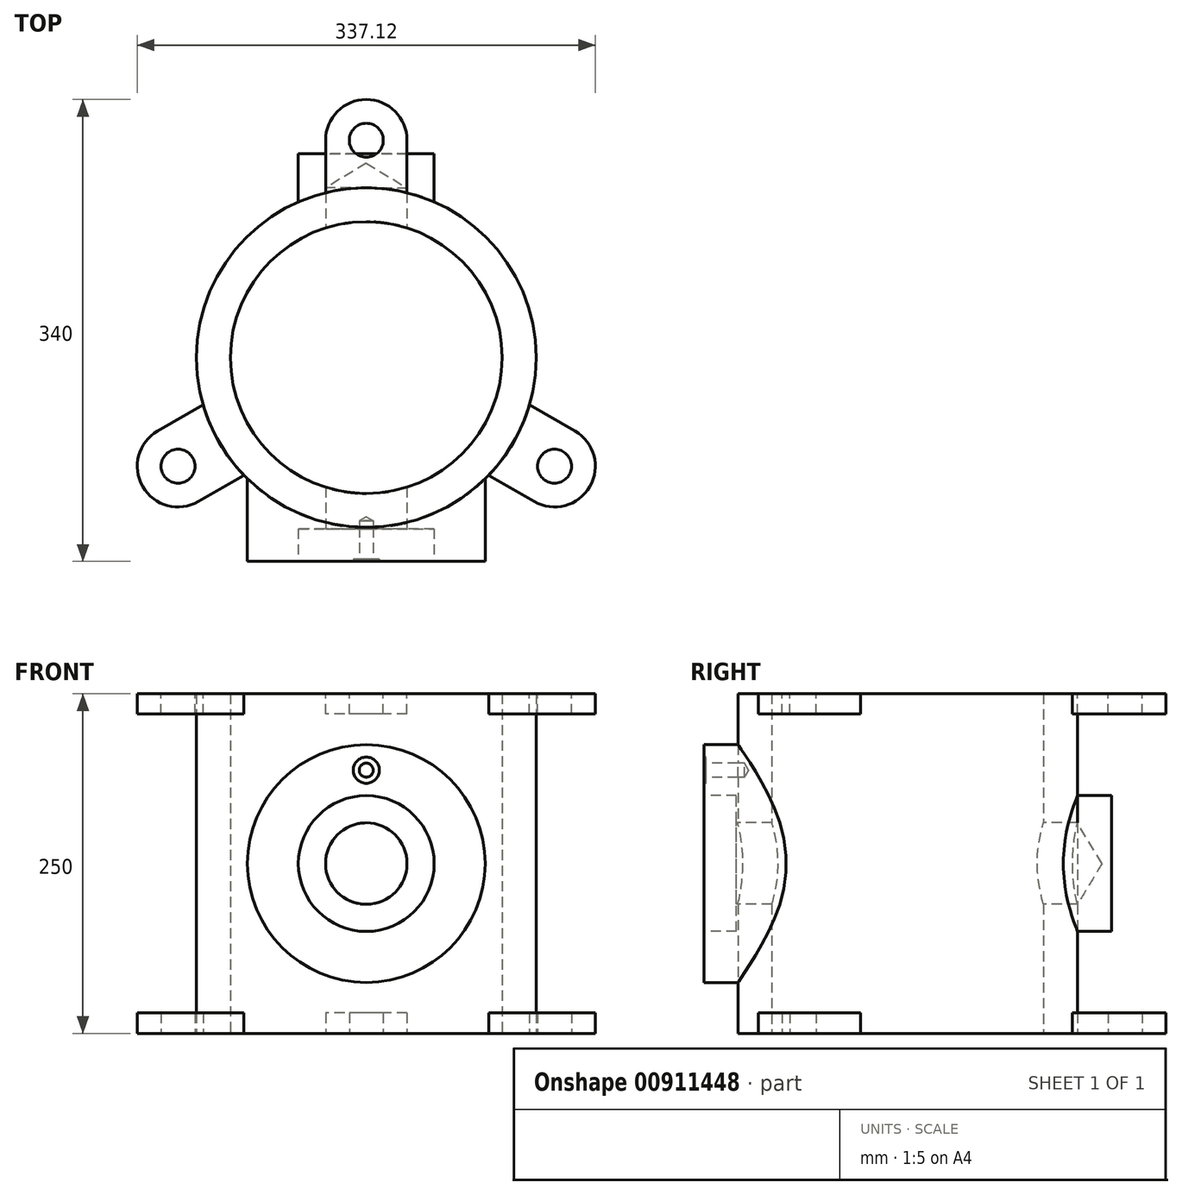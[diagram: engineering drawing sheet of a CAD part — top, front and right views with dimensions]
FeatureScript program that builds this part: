
annotation { "Feature Type Name" : "Feature", "Feature Type Description" : "" }
export const myFeature = defineFeature(function(context is Context, id is Id, definition is map)
    precondition{}
    {
        {
            var Q0;
            Q0=qCreatedBy(makeId("Top.planeOp"),FACE);
            var sketch = newSketch(context, id + "F0", { "sketchPlane" : qUnion([Q0])});
            skCircle(sketch, "E0", {"center": v(0, 0) * mm, "radius": 100 * mm});
            skCircle(sketch, "E1", {"center": v(0, 0) * mm, "radius": 125 * mm});
            skSolve(sketch);
        }
        {
            var Q0;
            Q0=makeQuery(id+"F0.imprint","IMPRINT",FACE,{"disambiguationData":[TD([[makeQuery(id+"F0.imprint","IMPRINT",EDGE,{"derivedFrom":sQuery(id+"F0.wireOp",EDGE,"E0")}),-1.0]])]});
            extrude(context, id + "F1", {"entities" : qUnion([Q0]), "depth" : 250 * mm, "offsetDistance" : 25 * mm, "symmetric" : true});
        }
        {
            var Q0;
            Q0=makeQuery(id+"F1.opExtrude","CAP_FACE",FACE,{"disambiguationData":[OSD([sQuery(id+"F0.wireOp",EDGE,"E0"),sQuery(id+"F0.wireOp",EDGE,"E1")])],"isStart":false});
            var sketch = newSketch(context, id + "F2", { "sketchPlane" : qUnion([Q0])});
            skLineSegment(sketch, "E2", {"start": v(0, 0) * mm, "end": v(0, 160) * mm, "construction": true});
            skCircle(sketch, "E3", {"center": v(0, 160) * mm, "radius": 12.5 * mm});
            skArc(sketch, "E4", {"start": v(-30, 160) * mm, "mid": v(0, 190) * mm, "end": v(30, 160) * mm});
            skLineSegment(sketch, "E5", {"start": v(30, 160) * mm, "end": v(30, 121.35) * mm});
            skLineSegment(sketch, "E6", {"start": v(-30, 160) * mm, "end": v(-30, 121.35) * mm});
            skLineSegment(sketch, "E7.1.0", {"start": v(-123.56, -105.98) * mm, "end": v(-90.09, -86.65) * mm});
            skCircle(sketch, "E7.1.1", {"center": v(-138.56, -80) * mm, "radius": 12.5 * mm});
            skLineSegment(sketch, "E7.1.2", {"start": v(-153.56, -54.02) * mm, "end": v(-120.09, -34.7) * mm});
            skArc(sketch, "E7.1.3", {"start": v(-123.56, -105.98) * mm, "mid": v(-164.54, -95) * mm, "end": v(-153.56, -54.02) * mm});
            skLineSegment(sketch, "E7.2.0", {"start": v(153.56, -54.02) * mm, "end": v(120.09, -34.7) * mm});
            skCircle(sketch, "E7.2.1", {"center": v(138.56, -80) * mm, "radius": 12.5 * mm});
            skLineSegment(sketch, "E7.2.2", {"start": v(123.56, -105.98) * mm, "end": v(90.09, -86.65) * mm});
            skArc(sketch, "E7.2.3", {"start": v(153.56, -54.02) * mm, "mid": v(164.54, -95) * mm, "end": v(123.56, -105.98) * mm});
            skPoint(sketch, "E7.center", {"position": v(0, 0) * mm});
            skSolve(sketch);
        }
        {
            var Q0;
            Q0=makeQuery(id+"F2.imprint","IMPRINT",FACE,{"disambiguationData":[TD([[makeQuery(id+"F2.imprint","IMPRINT",EDGE,{"derivedFrom":sQuery(id+"F2.wireOp",EDGE,"E3")}),-1.0]])]});
            var Q1;
            {var subQ1=sQuery(id+"F2.wireOp",EDGE,"E7.1.0");Q1=makeQuery(id+"F2.imprint","IMPRINT",FACE,{"disambiguationData":[TD([[makeQuery(id+"F2.imprint","IMPRINT",EDGE,{"derivedFrom":subQ1}),1.0]])]});}
            var Q2;
            {var subQ1=sQuery(id+"F2.wireOp",EDGE,"E7.2.0");Q2=makeQuery(id+"F2.imprint","IMPRINT",FACE,{"disambiguationData":[TD([[makeQuery(id+"F2.imprint","IMPRINT",EDGE,{"derivedFrom":subQ1}),1.0]])]});}
            extrude(context, id + "F3", {"entities" : qUnion([Q0, Q1, Q2]), "oppositeDirection" : true, "depth" : 15 * mm, "offsetDistance" : 25 * mm});
        }
        {
            var Q0;
            Q0=makeQuery(id+"F3.opExtrude","SWEPT_BODY",BODY,{"disambiguationData":[OSD([sQuery(id+"F0.wireOp",EDGE,"E1"),sQuery(id+"F2.wireOp",EDGE,"E3"),sQuery(id+"F2.wireOp",EDGE,"E4"),sQuery(id+"F2.wireOp",EDGE,"E5"),sQuery(id+"F2.wireOp",EDGE,"E6")])]});
            var Q1;
            Q1=makeQuery(id+"F3.opExtrude","SWEPT_BODY",BODY,{"disambiguationData":[OSD([sQuery(id+"F0.wireOp",EDGE,"E1"),sQuery(id+"F2.wireOp",EDGE,"E7.1.0"),sQuery(id+"F2.wireOp",EDGE,"E7.1.1"),sQuery(id+"F2.wireOp",EDGE,"E7.1.2"),sQuery(id+"F2.wireOp",EDGE,"E7.1.3")])]});
            var Q2;
            Q2=makeQuery(id+"F3.opExtrude","SWEPT_BODY",BODY,{"disambiguationData":[OSD([sQuery(id+"F0.wireOp",EDGE,"E1"),sQuery(id+"F2.wireOp",EDGE,"E7.2.0"),sQuery(id+"F2.wireOp",EDGE,"E7.2.1"),sQuery(id+"F2.wireOp",EDGE,"E7.2.2"),sQuery(id+"F2.wireOp",EDGE,"E7.2.3")])]});
            var Q3;
            Q3=qCreatedBy(makeId("Top.planeOp"),FACE);
            mirror(context, id + "F4", {"entities" : qUnion([Q0, Q1, Q2]), "mirrorPlane" : qUnion([Q3])});
        }
        {
            var Q0;
            Q0=qCreatedBy(makeId("Front.planeOp"),FACE);
            cPlane(context, id + "F5", {"entities" : qUnion([Q0]), "cplaneType" : CPlaneType.OFFSET, "offset" : 150 * mm, "width" : 150 * mm, "height" : 150 * mm});
        }
        {
            var Q0;
            Q0=qCreatedBy(id+"F5.planeOp",FACE);
            var sketch = newSketch(context, id + "F6", { "sketchPlane" : qUnion([Q0])});
            skCircle(sketch, "E8", {"center": v(0, 0) * mm, "radius": 87.5 * mm});
            skSolve(sketch);
        }
        {
            var Q0;
            Q0=makeQuery(id+"F6.imprint","IMPRINT",FACE,{"disambiguationData":[TD([[makeQuery(id+"F6.imprint","IMPRINT",EDGE,{"derivedFrom":sQuery(id+"F6.wireOp",EDGE,"E8")}),1.0]])]});
            extrude(context, id + "F7", {"entities" : qUnion([Q0]), "endBound" : BoundingType.UP_TO_NEXT, "oppositeDirection" : true, "depth" : 25 * mm, "offsetDistance" : 25 * mm});
        }
        {
            var Q0;
            Q0=qCreatedBy(makeId("Front.planeOp"),FACE);
            cPlane(context, id + "F8", {"entities" : qUnion([Q0]), "cplaneType" : CPlaneType.OFFSET, "offset" : 150 * mm, "oppositeDirection" : true, "width" : 150 * mm, "height" : 150 * mm});
        }
        {
            var Q0;
            Q0=qCreatedBy(id+"F8.planeOp",FACE);
            var sketch = newSketch(context, id + "F9", { "sketchPlane" : qUnion([Q0])});
            skCircle(sketch, "E9", {"center": v(0, 0) * mm, "radius": 50 * mm});
            skSolve(sketch);
        }
        {
            var Q0;
            Q0=makeQuery(id+"F9.imprint","IMPRINT",FACE,{"disambiguationData":[TD([[makeQuery(id+"F9.imprint","IMPRINT",EDGE,{"derivedFrom":sQuery(id+"F9.wireOp",EDGE,"E9")}),1.0]])]});
            extrude(context, id + "F10", {"entities" : qUnion([Q0]), "endBound" : BoundingType.UP_TO_NEXT, "depth" : 25 * mm, "offsetDistance" : 25 * mm});
        }
        {
            var Q0;
            Q0=qCreatedBy(id+"F5.planeOp",FACE);
            var sketch = newSketch(context, id + "F11", { "sketchPlane" : qUnion([Q0])});
            skPoint(sketch, "E10", {"position": v(0, 0) * mm});
            skPoint(sketch, "E11", {"position": v(0, 68.75) * mm});
            skSolve(sketch);
        }
        {
            var Q0;
            Q0=sQuery(id+"F11.wireOp",VERTEX,"E10");
            var Q1;
            Q1=makeQuery(id+"F1.opExtrude","SWEPT_BODY",BODY,{"disambiguationData":[OSD([sQuery(id+"F0.wireOp",EDGE,"E0"),sQuery(id+"F0.wireOp",EDGE,"E1")])]});
            var Q2;
            Q2=makeQuery(id+"FjgMNlp9pOEb26B_1.1.F1.opExtrude","SWEPT_BODY",BODY,{"disambiguationData":[OSD([sQuery(id+"F0.wireOp",EDGE,"E0"),sQuery(id+"F0.wireOp",EDGE,"E1")])]});
            var Q3;
            Q3=makeQuery(id+"FjgMNlp9pOEb26B_1.2.F1.opExtrude","SWEPT_BODY",BODY,{"disambiguationData":[OSD([sQuery(id+"F0.wireOp",EDGE,"E0"),sQuery(id+"F0.wireOp",EDGE,"E1")])]});
            var Q4;
            Q4=makeQuery(id+"F7.opExtrude","SWEPT_BODY",BODY,{"disambiguationData":[OSD([sQuery(id+"F6.wireOp",EDGE,"E8")])]});
            var Q5;
            Q5=makeQuery(id+"F10.opExtrude","SWEPT_BODY",BODY,{"disambiguationData":[OSD([sQuery(id+"F9.wireOp",EDGE,"E9")])]});
            hole(context, id + "F12", {"style" : HoleStyle.C_BORE, "endStyle" : HoleEndStyle.BLIND, "holeDiameter" : 60 * mm, "cBoreDiameter" : 100 * mm, "cBoreDepth" : 24 * mm, "majorDiameter" : 5 * mm, "holeDepth" : 275 * mm, "isTappedThrough" : true, "tappedDepth" : 12 * mm, "tapClearance" : 3, "locations" : qUnion([Q0]), "scope" : qUnion([Q1, Q2, Q3, Q4, Q5])});
        }
        {
            var Q0;
            Q0=qCreatedBy(id+"F5.planeOp",FACE);
            var sketch = newSketch(context, id + "F13", { "sketchPlane" : qUnion([Q0])});
            skPoint(sketch, "E12", {"position": v(0, 0) * mm});
            skPoint(sketch, "E13", {"position": v(0, 68.75) * mm});
            skSolve(sketch);
        }
        {
            var Q0;
            Q0=sQuery(id+"F13.wireOp",VERTEX,"E13");
            var Q1;
            Q1=makeQuery(id+"F1.opExtrude","SWEPT_BODY",BODY,{"disambiguationData":[OSD([sQuery(id+"F0.wireOp",EDGE,"E0"),sQuery(id+"F0.wireOp",EDGE,"E1")])]});
            var Q2;
            Q2=makeQuery(id+"FjgMNlp9pOEb26B_1.1.F1.opExtrude","SWEPT_BODY",BODY,{"disambiguationData":[OSD([sQuery(id+"F0.wireOp",EDGE,"E0"),sQuery(id+"F0.wireOp",EDGE,"E1")])]});
            var Q3;
            Q3=makeQuery(id+"FjgMNlp9pOEb26B_1.2.F1.opExtrude","SWEPT_BODY",BODY,{"disambiguationData":[OSD([sQuery(id+"F0.wireOp",EDGE,"E0"),sQuery(id+"F0.wireOp",EDGE,"E1")])]});
            var Q4;
            Q4=makeQuery(id+"F7.opExtrude","SWEPT_BODY",BODY,{"disambiguationData":[OSD([sQuery(id+"F6.wireOp",EDGE,"E8")])]});
            hole(context, id + "F14", {"style" : HoleStyle.C_BORE, "endStyle" : HoleEndStyle.BLIND, "holeDiameter" : 10.3 * mm, "cBoreDiameter" : 19.25 * mm, "cBoreDepth" : 1.75 * mm, "majorDiameter" : 5 * mm, "holeDepth" : 29.75 * mm, "isTappedThrough" : true, "tappedDepth" : 12 * mm, "tapClearance" : 3, "locations" : qUnion([Q0]), "scope" : qUnion([Q1, Q2, Q3, Q4])});
        }
    });
